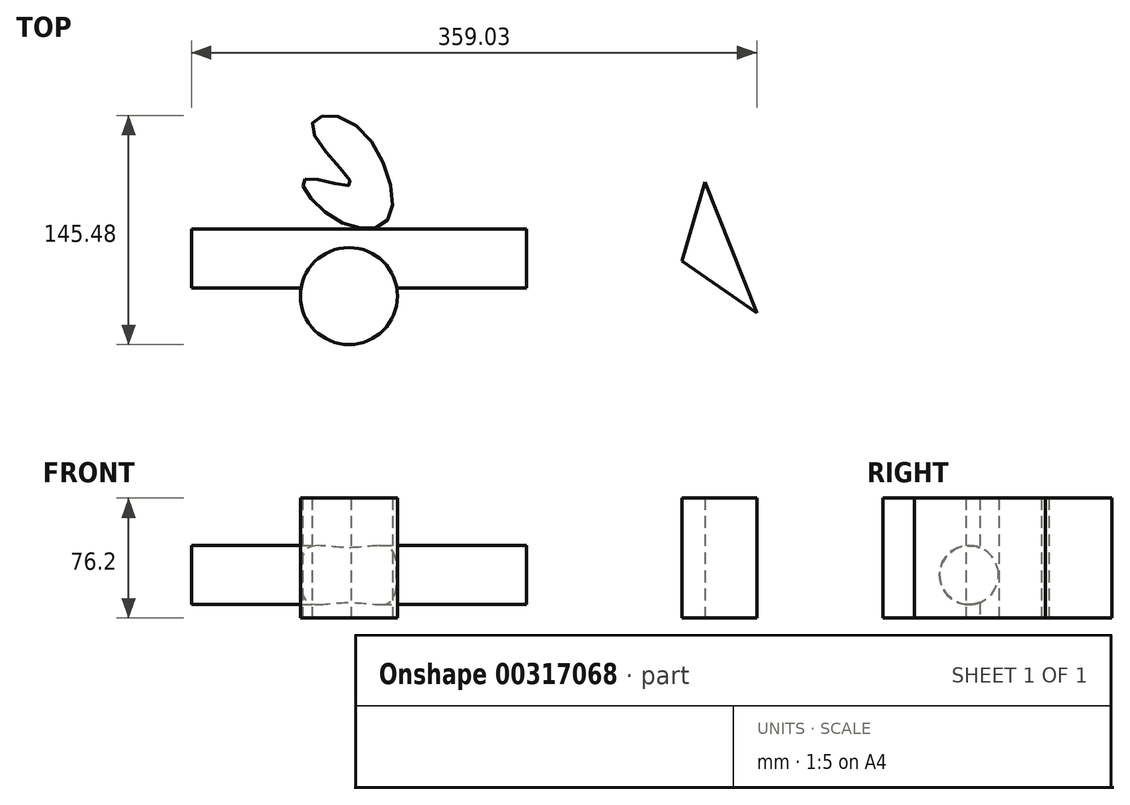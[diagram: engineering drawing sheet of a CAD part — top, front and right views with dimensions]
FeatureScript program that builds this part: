
annotation { "Feature Type Name" : "Feature", "Feature Type Description" : "" }
export const myFeature = defineFeature(function(context is Context, id is Id, definition is map)
    precondition{}
    {
        {
            var Q0;
            Q0=qCreatedBy(makeId("Top.planeOp"),FACE);
            var sketch = newSketch(context, id + "F0", { "sketchPlane" : qUnion([Q0])});
            skCircle(sketch, "E0", {"center": v(-112.65, -49.97) * mm, "radius": 30.81 * mm});
            skFitSpline(sketch, "E1", {"points": [v(-140.49, 24.34) * mm, v(-111.46, 20.66) * mm, v(-136.18, 56.96) * mm, v(-111.35, 60.53) * mm, v(-87.05, 0) * mm, v(-123.16, 0) * mm, v(-140.49, 24.34) * mm]});
            skLineSegment(sketch, "E2", {"start": v(146.43, -60.72) * mm, "end": v(113.46, 22.47) * mm});
            skLineSegment(sketch, "E3", {"start": v(113.46, 22.47) * mm, "end": v(98.95, -27.88) * mm});
            skLineSegment(sketch, "E4", {"start": v(98.95, -27.88) * mm, "end": v(146.43, -60.72) * mm});
            skLineSegment(sketch, "E5", {"start": v(-119.5, -49.97) * mm, "end": v(-119.5, -60.72) * mm});
            skLineSegment(sketch, "E6", {"start": v(-119.5, -60.72) * mm, "end": v(-119.5, -68.74) * mm});
            skSolve(sketch);
        }
        {
            var Q0;
            Q0=makeQuery(id+"F0.imprint","IMPRINT",FACE,{"disambiguationData":[TD([[makeQuery(id+"F0.imprint","IMPRINT",EDGE,{"derivedFrom":sQuery(id+"F0.wireOp",EDGE,"E0")}),1.0]])]});
            var Q1;
            Q1=makeQuery(id+"F0.imprint","IMPRINT",FACE,{"disambiguationData":[TD([[makeQuery(id+"F0.imprint","IMPRINT",EDGE,{"derivedFrom":sQuery(id+"F0.wireOp",EDGE,"E1")}),-1.0]])]});
            var Q2;
            Q2=makeQuery(id+"F0.imprint","IMPRINT",FACE,{"disambiguationData":[TD([[makeQuery(id+"F0.imprint","IMPRINT",EDGE,{"derivedFrom":sQuery(id+"F0.wireOp",EDGE,"E2")}),1.0]])]});
            extrude(context, id + "F1", {"entities" : qUnion([Q0, Q1, Q2]), "depth" : 76.2 * mm});
        }
        {
            var Q0;
            Q0=qCreatedBy(makeId("Right.planeOp"),FACE);
            var sketch = newSketch(context, id + "F2", { "sketchPlane" : qUnion([Q0])});
            skCircle(sketch, "E7", {"center": v(-26.04, 27.25) * mm, "radius": 18.7 * mm});
            skSolve(sketch);
        }
        {
            var Q0;
            Q0=makeQuery(id+"F2.imprint","IMPRINT",FACE,{"disambiguationData":[TD([[makeQuery(id+"F2.imprint","IMPRINT",EDGE,{"derivedFrom":sQuery(id+"F2.wireOp",EDGE,"E7")}),1.0]])]});
            extrude(context, id + "F3", {"entities" : qUnion([Q0]), "operationType" : NewBodyOperationType.ADD, "oppositeDirection" : true, "depth" : 212.6 * mm});
        }
    });
